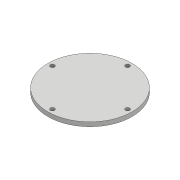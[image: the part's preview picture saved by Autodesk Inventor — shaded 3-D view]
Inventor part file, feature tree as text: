
AUTODESK INVENTOR PART (.ipt)
format: ipt  version: 2017 (Build 210142000, 142)  size: 83,456 bytes
history: native  units: mm
features: extrude x1, sketch x1
ambient origin geometry x8: Origin, YZ Plane, XZ Plane, XY Plane, X Axis, Y Axis, Z Axis, Center Point
bodies: Solid1 (feature_tree)
feature tree (2):
  extrude  "Extrusion1"  Depth=10.0mm
  sketch  "Sketch1"  dims[d0=200.0mm d1=10.0mm d2=40.0mm d4=360.0deg d6=10.0mm d7=0.0mm]
